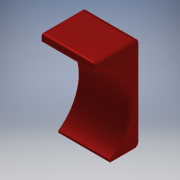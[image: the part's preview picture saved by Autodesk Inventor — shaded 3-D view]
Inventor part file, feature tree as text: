
AUTODESK INVENTOR PART (.ipt)
format: ipt  version: 2018 (Build 220112000, 112)  size: 164,864 bytes
history: native  units: mm
features: sketch x2, extrude x1, hole x1, fillet x1, chamfer x1, projected_geometry x1
ambient origin geometry x8: Origin, YZ Plane, XZ Plane, XY Plane, X Axis, Y Axis, Z Axis, Center Point
bodies: Solid1 (feature_tree)
feature tree (7):
  extrude  "Extrusion1"  Depth=18.3mm
  hole  "Hole1"  [1 undecoded]
  fillet  "Fillet1"  Radius=7.313mm
  chamfer  "Chamfer1"  Distance=2.0mm
  sketch  "Sketch1"  dims[d0=10.9mm d1=18.3mm]
  sketch  "Sketch2"  dims[d2=0.1mm d6=8.0mm d7=7.313mm d9=2.0mm d10=10.4mm d11=0.0mm d12=2.459mm d13=6.0mm d14=4.0mm d15=2.0mm d16=90.0deg d17=8.0mm d18=20.594885mm d19=10.5mm d20=1.0mm d21=0.5mm d22=0.25mm d23=16.0mm d24=0.0mm d25=0.25mm d26=2.0mm d27=45.0deg]
  projected_geometry  "Projected Loop1"
note: 1 required parameter value undecoded (feature->parameter linkage not recoverable at this tier; creation-order binding heuristic only, values carry confidence <= 0.55)
